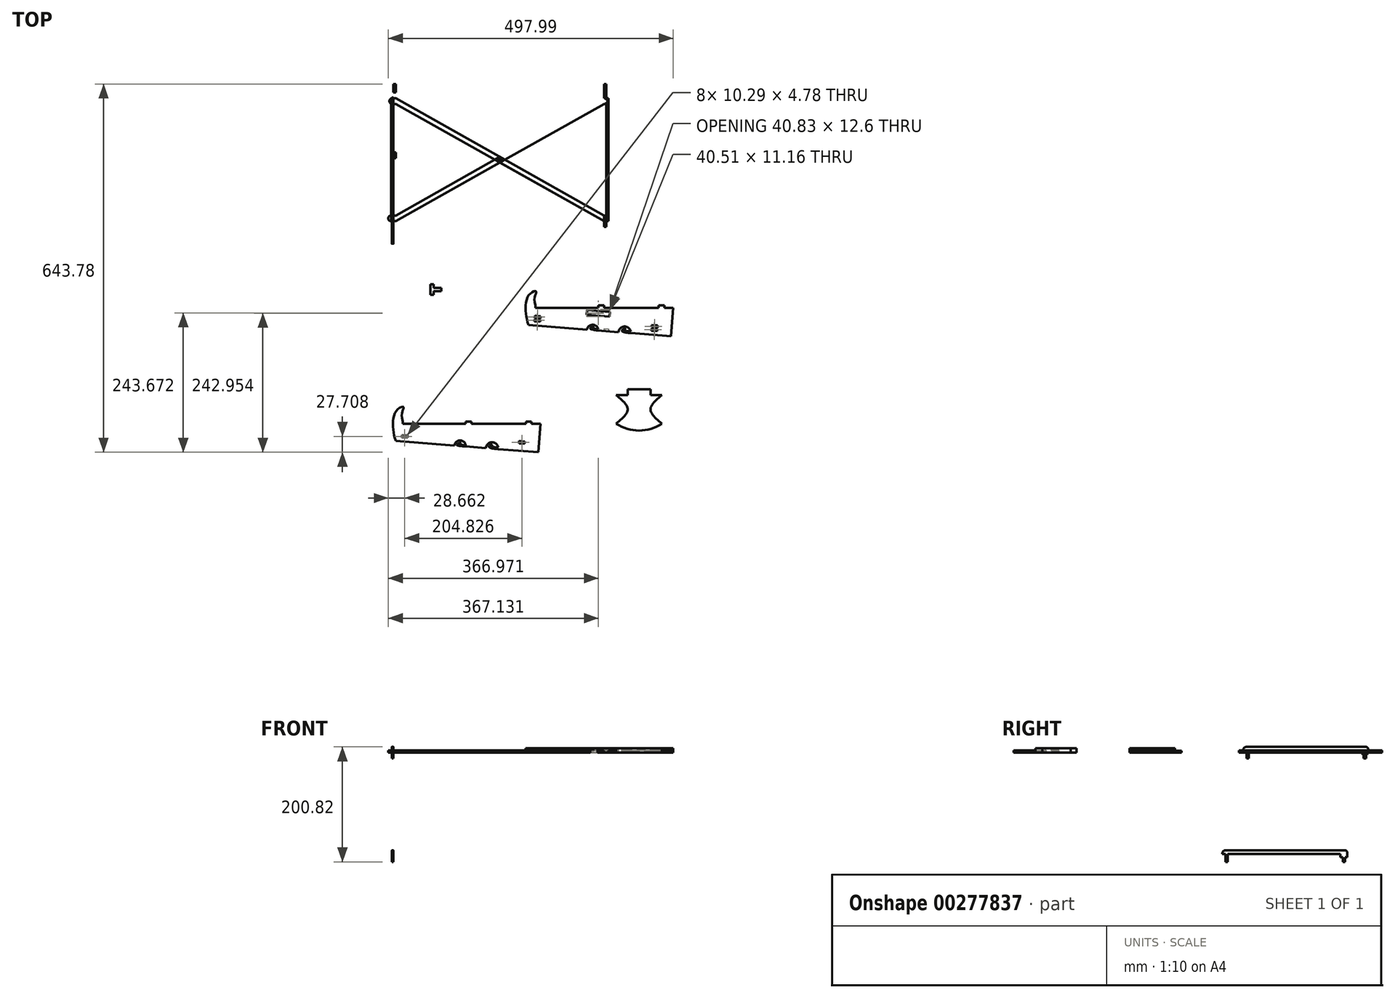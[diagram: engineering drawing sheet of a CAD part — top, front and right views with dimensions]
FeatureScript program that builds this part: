
annotation { "Feature Type Name" : "Feature", "Feature Type Description" : "" }
export const myFeature = defineFeature(function(context is Context, id is Id, definition is map)
    precondition{}
    {
        {
            var Q0;
            Q0=qCreatedBy(makeId("Top.planeOp"),FACE);
            var sketch = newSketch(context, id + "F0", { "sketchPlane" : qUnion([Q0])});
            skLineSegment(sketch, "E0.bottom", {"start": v(190, 125) * mm, "end": v(-190, 125) * mm});
            skLineSegment(sketch, "E0.top", {"start": v(190, -125) * mm, "end": v(-190, -125) * mm});
            skLineSegment(sketch, "E0.left", {"start": v(190, 125) * mm, "end": v(190, -125) * mm});
            skLineSegment(sketch, "E0.right", {"start": v(-190, 125) * mm, "end": v(-190, -125) * mm});
            skPoint(sketch, "E0.middle", {"position": v(0, 0) * mm});
            skLineSegment(sketch, "E1.right", {"start": v(-190, 125) * mm, "end": v(-190, -108) * mm});
            skLineSegment(sketch, "E2.bottom", {"start": v(-190, -125) * mm, "end": v(-186, -125) * mm});
            skLineSegment(sketch, "E2.top", {"start": v(-190, 125) * mm, "end": v(-186, 125) * mm});
            skLineSegment(sketch, "E2.left", {"start": v(-190, -125) * mm, "end": v(-190, -112) * mm});
            skLineSegment(sketch, "E2.right", {"start": v(-186, -125) * mm, "end": v(-186, -115) * mm});
            skLineSegment(sketch, "E3.bottom", {"start": v(190, -125) * mm, "end": v(186, -125) * mm});
            skLineSegment(sketch, "E3.top", {"start": v(190, 125) * mm, "end": v(186, 125) * mm});
            skLineSegment(sketch, "E3.left", {"start": v(190, -125) * mm, "end": v(190, 125) * mm});
            skLineSegment(sketch, "E3.right", {"start": v(186, -125) * mm, "end": v(186, 125) * mm});
            skLineSegment(sketch, "E4", {"start": v(49.8, -296.15) * mm, "end": v(152.32, -304.35) * mm});
            skLineSegment(sketch, "E5", {"start": v(299, -316.08) * mm, "end": v(303, -266.24) * mm});
            skLineSegment(sketch, "E6", {"start": v(303, -266.24) * mm, "end": v(287.2, -266.24) * mm});
            skLineSegment(sketch, "E7", {"start": v(52.2, -266.24) * mm, "end": v(49.8, -296.15) * mm, "construction": true});
            skLineSegment(sketch, "E8", {"start": v(0, 0) * mm, "end": v(0, 125) * mm, "construction": true});
            skLineSegment(sketch, "E9", {"start": v(0, 0) * mm, "end": v(0, -125) * mm, "construction": true});
            skLineSegment(sketch, "E10.bottom", {"start": v(-186, 125) * mm, "end": v(-182, 125) * mm});
            skLineSegment(sketch, "E10.top", {"start": v(-186, -125) * mm, "end": v(-182, -125) * mm});
            skLineSegment(sketch, "E10.left", {"start": v(-186, 125) * mm, "end": v(-186, 100) * mm});
            skLineSegment(sketch, "E10.right", {"start": v(-182, 125) * mm, "end": v(-182, 100) * mm});
            skLineSegment(sketch, "E11.MirrorCS", {"start": v(182, 125) * mm, "end": v(182, -125) * mm});
            skLineSegment(sketch, "E12", {"start": v(-186, -115) * mm, "end": v(-182, -115) * mm});
            skLineSegment(sketch, "E13", {"start": v(-186, 0) * mm, "end": v(186, 0) * mm, "construction": true});
            skLineSegment(sketch, "E14", {"start": v(-183.8, 0) * mm, "end": v(-183.8, 5) * mm, "construction": true});
            skLineSegment(sketch, "E15", {"start": v(-186, 5) * mm, "end": v(-182, 5) * mm});
            skLineSegment(sketch, "E16.MirrorCS", {"start": v(-186, -5) * mm, "end": v(-182, -5) * mm});
            skLineSegment(sketch, "E17", {"start": v(-186, 110) * mm, "end": v(-182, 110) * mm});
            skLineSegment(sketch, "E18", {"start": v(-186, 100) * mm, "end": v(-182, 100) * mm});
            skLineSegment(sketch, "E19", {"start": v(52.2, -266.24) * mm, "end": v(52.2, -242.24) * mm, "construction": true});
            skLineSegment(sketch, "E20", {"start": v(52.2, -242.24) * mm, "end": v(62.16, -243.04) * mm, "construction": true});
            skLineSegment(sketch, "E21", {"start": v(62.16, -243.04) * mm, "end": v(62.16, -266.24) * mm, "construction": true});
            skLineSegment(sketch, "E22.bottom", {"start": v(62.16, -266.24) * mm, "end": v(172.2, -266.24) * mm, "construction": true});
            skLineSegment(sketch, "E22.top", {"start": v(52.2, -262.24) * mm, "end": v(303, -262.24) * mm, "construction": true});
            skLineSegment(sketch, "E22.left", {"start": v(52.2, -266.24) * mm, "end": v(52.2, -262.24) * mm, "construction": true});
            skLineSegment(sketch, "E22.right", {"start": v(303, -266.24) * mm, "end": v(303, -262.24) * mm, "construction": true});
            skFitSpline(sketch, "E23", {"points": [v(49.8, -296.15) * mm, v(44.72, -265.8) * mm, v(52.2, -242.24) * mm, v(62.86, -237.24) * mm, v(62.38, -242.24) * mm, v(62.16, -262.24) * mm], "startDerivative": vector(-32.9, 108.57) * mm, "endDerivative": vector(52.9, -154.73) * mm});
            skLineSegment(sketch, "E24", {"start": v(62.16, -262.24) * mm, "end": v(62.16, -266.24) * mm});
            skLineSegment(sketch, "E25", {"start": v(302.2, -266.24) * mm, "end": v(302.2, -262.24) * mm, "construction": true});
            skLineSegment(sketch, "E26", {"start": v(287.2, -266.24) * mm, "end": v(287.2, -262.24) * mm});
            skLineSegment(sketch, "E27", {"start": v(287.2, -262.24) * mm, "end": v(277.2, -262.24) * mm});
            skLineSegment(sketch, "E28", {"start": v(277.2, -262.24) * mm, "end": v(277.2, -266.24) * mm});
            skLineSegment(sketch, "E29", {"start": v(182.2, -266.24) * mm, "end": v(182.2, -262.24) * mm});
            skLineSegment(sketch, "E30", {"start": v(172.2, -266.24) * mm, "end": v(172.2, -262.24) * mm});
            skLineSegment(sketch, "E31", {"start": v(172.2, -262.24) * mm, "end": v(182.2, -262.24) * mm});
            skLineSegment(sketch, "E32", {"start": v(-182, -105) * mm, "end": v(-186, -105) * mm});
            skLineSegment(sketch, "E33", {"start": v(-186, 90) * mm, "end": v(-182, 90) * mm});
            skLineSegment(sketch, "E34.MirrorCS", {"start": v(186, 125) * mm, "end": v(182, 125) * mm});
            skLineSegment(sketch, "E35.MirrorCS", {"start": v(186, -125) * mm, "end": v(182, -125) * mm});
            skLineSegment(sketch, "E36.MirrorCS", {"start": v(-190, -125) * mm, "end": v(190, -125) * mm});
            skLineSegment(sketch, "E37.MirrorCS", {"start": v(186, 110) * mm, "end": v(182, 110) * mm});
            skLineSegment(sketch, "E38.MirrorCS", {"start": v(183.8, 0) * mm, "end": v(183.8, 5) * mm, "construction": true});
            skLineSegment(sketch, "E39.MirrorCS", {"start": v(186, 100) * mm, "end": v(182, 100) * mm});
            skLineSegment(sketch, "E40.MirrorCS", {"start": v(182, -105) * mm, "end": v(186, -105) * mm});
            skLineSegment(sketch, "E41.MirrorCS", {"start": v(186, -5) * mm, "end": v(182, -5) * mm});
            skLineSegment(sketch, "E42.MirrorCS", {"start": v(186, 90) * mm, "end": v(182, 90) * mm});
            skLineSegment(sketch, "E43.MirrorCS", {"start": v(186, 5) * mm, "end": v(182, 5) * mm});
            skLineSegment(sketch, "E44.MirrorCS", {"start": v(186, -115) * mm, "end": v(182, -115) * mm});
            skLineSegment(sketch, "E45", {"start": v(-182, -115) * mm, "end": v(182, 90) * mm});
            skLineSegment(sketch, "E46", {"start": v(-182, -105) * mm, "end": v(182, 100) * mm});
            skLineSegment(sketch, "E47", {"start": v(-182, 90) * mm, "end": v(182, -115) * mm});
            skLineSegment(sketch, "E48", {"start": v(182, -105) * mm, "end": v(-182, 100) * mm});
            skLineSegment(sketch, "E49.trimOffspring", {"start": v(-186, -115) * mm, "end": v(-186, -125) * mm});
            skLineSegment(sketch, "E50.trimOffspring", {"start": v(-186, -105) * mm, "end": v(-186, 90) * mm});
            skLineSegment(sketch, "E51", {"start": v(-186, -105) * mm, "end": v(-190, -105) * mm});
            skLineSegment(sketch, "E52", {"start": v(-186, -115) * mm, "end": v(-190, -115) * mm});
            skArc(sketch, "E53", {"start": v(-190, -105) * mm, "mid": v(-195, -110) * mm, "end": v(-190, -115) * mm});
            skArc(sketch, "E54", {"start": v(-190, 99.76) * mm, "mid": v(-193.01, 94.84) * mm, "end": v(-190, 89.93) * mm});
            skLineSegment(sketch, "E55.trimOffspring", {"start": v(-186, 100) * mm, "end": v(-186, 125) * mm});
            skLineSegment(sketch, "E56.trimOffspring", {"start": v(-186, 90) * mm, "end": v(-186, -105) * mm});
            skLineSegment(sketch, "E57.trimOffspring", {"start": v(-182, 90) * mm, "end": v(-182, -125) * mm});
            skLineSegment(sketch, "E58.MirrorCS", {"start": v(186, -125) * mm, "end": v(186, -115) * mm});
            skLineSegment(sketch, "E59.MirrorCS", {"start": v(186, -115) * mm, "end": v(186, -125) * mm});
            skLineSegment(sketch, "E60.MirrorCS", {"start": v(186, -115) * mm, "end": v(190, -115) * mm});
            skLineSegment(sketch, "E61.MirrorCS", {"start": v(186, -105) * mm, "end": v(190, -105) * mm});
            skArc(sketch, "E62.MirrorCS", {"start": v(190, -105) * mm, "mid": v(195, -110) * mm, "end": v(190, -115) * mm});
            skLineSegment(sketch, "E63.MirrorCS", {"start": v(186, 100) * mm, "end": v(186, 125) * mm});
            skLineSegment(sketch, "E64.MirrorCS", {"start": v(182, 125) * mm, "end": v(182, 100) * mm});
            skLineSegment(sketch, "E65.MirrorCS", {"start": v(186, 125) * mm, "end": v(186, 100) * mm});
            skArc(sketch, "E66.MirrorCS", {"start": v(190, 99.76) * mm, "mid": v(193.01, 94.84) * mm, "end": v(190, 89.93) * mm});
            skLineSegment(sketch, "E67.MirrorCS", {"start": v(186, 90) * mm, "end": v(186, -105) * mm});
            skLineSegment(sketch, "E68.MirrorCS", {"start": v(186, -105) * mm, "end": v(186, 90) * mm});
            skLineSegment(sketch, "E69.MirrorCS", {"start": v(182, 90) * mm, "end": v(182, -125) * mm});
            skLineSegment(sketch, "E70", {"start": v(186, 100) * mm, "end": v(190, 99.76) * mm});
            skLineSegment(sketch, "E71", {"start": v(186, 90) * mm, "end": v(190, 89.93) * mm});
            skLineSegment(sketch, "E72", {"start": v(-186, 90) * mm, "end": v(-190, 89.93) * mm});
            skLineSegment(sketch, "E73", {"start": v(-186, 100) * mm, "end": v(-190, 99.76) * mm});
            skLineSegment(sketch, "E74.trimOffspring", {"start": v(182.2, -266.24) * mm, "end": v(277.2, -266.24) * mm, "construction": true});
            skLineSegment(sketch, "E75.trimOffspring", {"start": v(172.2, -266.24) * mm, "end": v(62.16, -266.24) * mm});
            skLineSegment(sketch, "E76.trimOffspring", {"start": v(287.2, -266.24) * mm, "end": v(303, -266.24) * mm, "construction": true});
            skLineSegment(sketch, "E77.trimOffspring", {"start": v(277.2, -266.24) * mm, "end": v(182.2, -266.24) * mm});
            skLineSegment(sketch, "E78", {"start": v(50.88, -283.2) * mm, "end": v(70.77, -284.78) * mm, "construction": true});
            skLineSegment(sketch, "E79", {"start": v(51.2, -279.2) * mm, "end": v(61.13, -280) * mm, "construction": true});
            skLineSegment(sketch, "E80", {"start": v(275.12, -301.13) * mm, "end": v(275.44, -297.14) * mm});
            skLineSegment(sketch, "E81", {"start": v(275.44, -297.14) * mm, "end": v(265.47, -296.35) * mm});
            skLineSegment(sketch, "E82", {"start": v(265.47, -296.35) * mm, "end": v(265.15, -300.33) * mm});
            skLineSegment(sketch, "E83", {"start": v(265.15, -300.33) * mm, "end": v(275.12, -301.13) * mm});
            skLineSegment(sketch, "E84", {"start": v(60.8, -283.99) * mm, "end": v(61.13, -280) * mm});
            skLineSegment(sketch, "E85", {"start": v(71.1, -280.8) * mm, "end": v(70.77, -284.78) * mm});
            skLineSegment(sketch, "E86", {"start": v(61.13, -280) * mm, "end": v(71.1, -280.8) * mm});
            skLineSegment(sketch, "E87", {"start": v(70.77, -284.78) * mm, "end": v(60.8, -283.99) * mm});
            skLineSegment(sketch, "E88", {"start": v(265.47, -296.35) * mm, "end": v(264.12, -313.3) * mm, "construction": true});
            skLineSegment(sketch, "E89", {"start": v(275.44, -297.14) * mm, "end": v(274.09, -314.1) * mm, "construction": true});
            skLineSegment(sketch, "E90", {"start": v(264.68, -306.32) * mm, "end": v(274.64, -307.11) * mm});
            skLineSegment(sketch, "E91", {"start": v(265, -302.33) * mm, "end": v(274.96, -303.13) * mm});
            skLineSegment(sketch, "E92", {"start": v(265, -302.33) * mm, "end": v(264.68, -306.32) * mm});
            skLineSegment(sketch, "E93", {"start": v(274.96, -303.13) * mm, "end": v(274.64, -307.11) * mm});
            skLineSegment(sketch, "E94", {"start": v(61.13, -280) * mm, "end": v(59.77, -296.95) * mm, "construction": true});
            skLineSegment(sketch, "E95", {"start": v(60.65, -285.98) * mm, "end": v(70.62, -286.78) * mm});
            skLineSegment(sketch, "E96", {"start": v(60.33, -289.97) * mm, "end": v(70.3, -290.77) * mm});
            skLineSegment(sketch, "E97", {"start": v(70.3, -290.77) * mm, "end": v(70.62, -286.78) * mm});
            skLineSegment(sketch, "E98", {"start": v(60.65, -285.98) * mm, "end": v(60.33, -289.97) * mm});
            skLineSegment(sketch, "E99", {"start": v(-182, -498.85) * mm, "end": v(-79.55, -507.04) * mm});
            skLineSegment(sketch, "E100", {"start": v(67.2, -518.78) * mm, "end": v(71.18, -468.94) * mm});
            skLineSegment(sketch, "E101", {"start": v(71.18, -468.94) * mm, "end": v(55.38, -468.94) * mm});
            skLineSegment(sketch, "E102", {"start": v(-179.62, -468.94) * mm, "end": v(-182, -498.85) * mm, "construction": true});
            skLineSegment(sketch, "E103", {"start": v(-179.62, -468.94) * mm, "end": v(-179.62, -444.94) * mm, "construction": true});
            skLineSegment(sketch, "E104", {"start": v(-179.62, -444.94) * mm, "end": v(-169.65, -445.74) * mm, "construction": true});
            skLineSegment(sketch, "E105", {"start": v(-169.65, -445.74) * mm, "end": v(-169.65, -468.94) * mm, "construction": true});
            skLineSegment(sketch, "E106.bottom", {"start": v(-169.65, -468.94) * mm, "end": v(-59.62, -468.94) * mm, "construction": true});
            skLineSegment(sketch, "E106.top", {"start": v(-179.62, -464.94) * mm, "end": v(71.18, -464.94) * mm, "construction": true});
            skLineSegment(sketch, "E106.left", {"start": v(-179.62, -468.94) * mm, "end": v(-179.62, -464.94) * mm, "construction": true});
            skLineSegment(sketch, "E106.right", {"start": v(71.18, -468.94) * mm, "end": v(71.18, -464.94) * mm, "construction": true});
            skFitSpline(sketch, "E107", {"points": [v(-182, -498.85) * mm, v(-187.09, -467.99) * mm, v(-179.62, -444.94) * mm, v(-168.95, -439.42) * mm, v(-169.43, -444.94) * mm, v(-169.65, -464.94) * mm], "startDerivative": vector(-32.9, 108.57) * mm, "endDerivative": vector(52.9, -154.73) * mm});
            skLineSegment(sketch, "E108", {"start": v(-169.65, -464.94) * mm, "end": v(-169.65, -468.94) * mm});
            skLineSegment(sketch, "E109", {"start": v(70.38, -468.94) * mm, "end": v(70.38, -464.94) * mm, "construction": true});
            skLineSegment(sketch, "E110", {"start": v(55.38, -468.94) * mm, "end": v(55.38, -464.94) * mm});
            skLineSegment(sketch, "E111", {"start": v(55.38, -464.94) * mm, "end": v(45.38, -464.94) * mm});
            skLineSegment(sketch, "E112", {"start": v(45.38, -464.94) * mm, "end": v(45.38, -468.94) * mm});
            skLineSegment(sketch, "E113", {"start": v(-49.62, -468.94) * mm, "end": v(-49.62, -464.94) * mm});
            skLineSegment(sketch, "E114", {"start": v(-59.62, -468.94) * mm, "end": v(-59.62, -464.94) * mm});
            skLineSegment(sketch, "E115", {"start": v(-59.62, -464.94) * mm, "end": v(-49.62, -464.94) * mm});
            skLineSegment(sketch, "E116.trimOffspring", {"start": v(-49.62, -468.94) * mm, "end": v(45.38, -468.94) * mm, "construction": true});
            skLineSegment(sketch, "E117.trimOffspring", {"start": v(-59.62, -468.94) * mm, "end": v(-169.65, -468.94) * mm});
            skLineSegment(sketch, "E118.trimOffspring", {"start": v(55.38, -468.94) * mm, "end": v(71.18, -468.94) * mm, "construction": true});
            skLineSegment(sketch, "E119.trimOffspring", {"start": v(45.38, -468.94) * mm, "end": v(-49.62, -468.94) * mm});
            skLineSegment(sketch, "E120", {"start": v(-180.97, -485.89) * mm, "end": v(68.23, -505.82) * mm, "construction": true});
            skLineSegment(sketch, "E121", {"start": v(-180.65, -481.9) * mm, "end": v(68.55, -501.84) * mm, "construction": true});
            skLineSegment(sketch, "E122", {"start": v(43.31, -503.83) * mm, "end": v(43.63, -499.84) * mm});
            skLineSegment(sketch, "E123", {"start": v(43.63, -499.84) * mm, "end": v(33.66, -499.05) * mm});
            skLineSegment(sketch, "E124", {"start": v(33.66, -499.05) * mm, "end": v(33.34, -503.03) * mm});
            skLineSegment(sketch, "E125", {"start": v(33.34, -503.03) * mm, "end": v(43.31, -503.83) * mm});
            skLineSegment(sketch, "E126", {"start": v(-171, -486.69) * mm, "end": v(-170.68, -482.7) * mm});
            skLineSegment(sketch, "E127", {"start": v(-160.72, -483.5) * mm, "end": v(-161.03, -487.48) * mm});
            skLineSegment(sketch, "E128", {"start": v(-170.68, -482.7) * mm, "end": v(-160.72, -483.5) * mm});
            skLineSegment(sketch, "E129", {"start": v(-161.03, -487.48) * mm, "end": v(-171, -486.69) * mm});
            skLineSegment(sketch, "E130", {"start": v(33.66, -499.05) * mm, "end": v(32.3, -516) * mm, "construction": true});
            skLineSegment(sketch, "E131", {"start": v(43.63, -499.84) * mm, "end": v(42.28, -516.79) * mm, "construction": true});
            skLineSegment(sketch, "E132", {"start": v(32.87, -509.01) * mm, "end": v(42.83, -509.81) * mm});
            skLineSegment(sketch, "E133", {"start": v(33.19, -505.03) * mm, "end": v(43.15, -505.82) * mm});
            skLineSegment(sketch, "E134", {"start": v(33.19, -505.03) * mm, "end": v(32.87, -509.01) * mm});
            skLineSegment(sketch, "E135", {"start": v(43.15, -505.82) * mm, "end": v(42.83, -509.81) * mm});
            skLineSegment(sketch, "E136", {"start": v(-170.68, -482.7) * mm, "end": v(-172.04, -499.64) * mm, "construction": true});
            skLineSegment(sketch, "E137", {"start": v(-171.16, -488.68) * mm, "end": v(-161.2, -489.48) * mm});
            skLineSegment(sketch, "E138", {"start": v(-171.48, -492.67) * mm, "end": v(-161.51, -493.46) * mm});
            skLineSegment(sketch, "E139", {"start": v(-161.51, -493.46) * mm, "end": v(-161.2, -489.48) * mm});
            skLineSegment(sketch, "E140", {"start": v(-171.16, -488.68) * mm, "end": v(-171.48, -492.67) * mm});
            skLineSegment(sketch, "E141.MirrorCS", {"start": v(-190, -125) * mm, "end": v(-190, 125) * mm});
            skLineSegment(sketch, "E142.trimOffspring", {"start": v(-190, -108) * mm, "end": v(-190, 125) * mm});
            skLineSegment(sketch, "E143.trimOffspring", {"start": v(-190, -110) * mm, "end": v(-190, -125) * mm});
            skLineSegment(sketch, "E144.bottom", {"start": v(-189, 96.84) * mm, "end": v(-186, 96.84) * mm, "construction": true});
            skLineSegment(sketch, "E144.top", {"start": v(-189, 92.84) * mm, "end": v(-186, 92.84) * mm, "construction": true});
            skLineSegment(sketch, "E144.left", {"start": v(-189, 96.84) * mm, "end": v(-189, 92.84) * mm, "construction": true});
            skLineSegment(sketch, "E144.right", {"start": v(-186, 96.84) * mm, "end": v(-186, 92.84) * mm, "construction": true});
            skLineSegment(sketch, "E145.MirrorCS", {"start": v(189, 92.84) * mm, "end": v(186, 92.84) * mm});
            skLineSegment(sketch, "E146.MirrorCS", {"start": v(189, 96.84) * mm, "end": v(186, 96.84) * mm});
            skLineSegment(sketch, "E147.MirrorCS", {"start": v(189, 96.84) * mm, "end": v(189, 92.84) * mm});
            skLineSegment(sketch, "E148.MirrorCS", {"start": v(186, 96.84) * mm, "end": v(186, 92.84) * mm});
            skLineSegment(sketch, "E149.bottom", {"start": v(-186.1, -112) * mm, "end": v(-189.1, -112) * mm});
            skLineSegment(sketch, "E149.top", {"start": v(-186.1, -108) * mm, "end": v(-189.1, -108) * mm});
            skLineSegment(sketch, "E149.left", {"start": v(-186.1, -112) * mm, "end": v(-186.1, -108) * mm});
            skLineSegment(sketch, "E149.right", {"start": v(-189.1, -112) * mm, "end": v(-189.1, -108) * mm});
            skLineSegment(sketch, "E150", {"start": v(-186, -105) * mm, "end": v(-186, -115) * mm, "construction": true});
            skLineSegment(sketch, "E151.MirrorCS", {"start": v(190, -108) * mm, "end": v(190, 125) * mm});
            skLineSegment(sketch, "E152.MirrorCS", {"start": v(190, -110) * mm, "end": v(190, -125) * mm});
            skLineSegment(sketch, "E153.MirrorCS", {"start": v(186, -105) * mm, "end": v(186, -115) * mm, "construction": true});
            skLineSegment(sketch, "E154.MirrorCS", {"start": v(190, 125) * mm, "end": v(190, -108) * mm});
            skLineSegment(sketch, "E155.MirrorCS", {"start": v(186.1, -112) * mm, "end": v(189.1, -112) * mm});
            skLineSegment(sketch, "E156.MirrorCS", {"start": v(190, -125) * mm, "end": v(190, -112) * mm});
            skLineSegment(sketch, "E157.MirrorCS", {"start": v(186.1, -112) * mm, "end": v(186.1, -108) * mm});
            skLineSegment(sketch, "E158.MirrorCS", {"start": v(189.1, -112) * mm, "end": v(189.1, -108) * mm});
            skLineSegment(sketch, "E159.MirrorCS", {"start": v(186.1, -108) * mm, "end": v(189.1, -108) * mm});
            skLineSegment(sketch, "E160", {"start": v(-186, 90) * mm, "end": v(-186, 100) * mm, "construction": true});
            skLineSegment(sketch, "E161.bottom", {"start": v(-189, 96.84) * mm, "end": v(-186, 96.84) * mm});
            skLineSegment(sketch, "E161.top", {"start": v(-189, 92.84) * mm, "end": v(-186, 92.84) * mm});
            skLineSegment(sketch, "E161.left", {"start": v(-189, 96.84) * mm, "end": v(-189, 92.84) * mm});
            skLineSegment(sketch, "E161.right", {"start": v(-186, 96.84) * mm, "end": v(-186, 92.84) * mm});
            skLineSegment(sketch, "E162", {"start": v(8.88, -7.5) * mm, "end": v(-8.88, -7.5) * mm, "construction": true});
            skLineSegment(sketch, "E163.bottom", {"start": v(3, -9) * mm, "end": v(-3, -9) * mm});
            skLineSegment(sketch, "E163.top", {"start": v(3, -6) * mm, "end": v(-3, -6) * mm});
            skLineSegment(sketch, "E163.left", {"start": v(3, -9) * mm, "end": v(3, -6) * mm});
            skLineSegment(sketch, "E163.right", {"start": v(-3, -9) * mm, "end": v(-3, -6) * mm});
            skPoint(sketch, "E163.middle", {"position": v(0, -7.5) * mm});
            skLineSegment(sketch, "E164.bottom", {"start": v(-115.58, -237.46) * mm, "end": v(-102.58, -237.46) * mm});
            skLineSegment(sketch, "E164.top", {"start": v(-115.58, -231.46) * mm, "end": v(-102.58, -231.46) * mm});
            skLineSegment(sketch, "E164.left", {"start": v(-121.58, -237.46) * mm, "end": v(-121.58, -231.46) * mm});
            skLineSegment(sketch, "E164.right", {"start": v(-102.58, -237.46) * mm, "end": v(-102.58, -231.46) * mm});
            skPoint(sketch, "E164.middle", {"position": v(-112.08, -234.46) * mm});
            skLineSegment(sketch, "E165.top", {"start": v(-121.58, -243.46) * mm, "end": v(-115.58, -243.46) * mm});
            skLineSegment(sketch, "E165.left", {"start": v(-121.58, -231.46) * mm, "end": v(-121.58, -243.46) * mm});
            skLineSegment(sketch, "E165.right", {"start": v(-115.58, -237.46) * mm, "end": v(-115.58, -243.46) * mm});
            skLineSegment(sketch, "E166", {"start": v(-105.58, -231.46) * mm, "end": v(-105.58, -237.46) * mm, "construction": true});
            skLineSegment(sketch, "E167", {"start": v(-121.58, -231.46) * mm, "end": v(-121.58, -225.46) * mm});
            skLineSegment(sketch, "E168", {"start": v(-121.58, -225.46) * mm, "end": v(-115.58, -225.46) * mm});
            skLineSegment(sketch, "E169", {"start": v(-115.58, -225.46) * mm, "end": v(-115.58, -231.46) * mm});
            skLineSegment(sketch, "E170", {"start": v(191.59, -281.4) * mm, "end": v(151.72, -278.22) * mm});
            skLineSegment(sketch, "E171", {"start": v(151.72, -278.22) * mm, "end": v(152.35, -270.24) * mm});
            skLineSegment(sketch, "E172", {"start": v(152.35, -270.24) * mm, "end": v(192.23, -273.43) * mm});
            skLineSegment(sketch, "E173", {"start": v(192.23, -273.43) * mm, "end": v(191.59, -281.4) * mm});
            skLineSegment(sketch, "E174.trimOffspring", {"start": v(237.81, -294.13) * mm, "end": v(300.4, -299.14) * mm, "construction": true});
            skLineSegment(sketch, "E175", {"start": v(181.86, -302.7) * mm, "end": v(189.85, -303.34) * mm});
            skLineSegment(sketch, "E176", {"start": v(181.54, -306.69) * mm, "end": v(197.49, -307.96) * mm});
            skLineSegment(sketch, "E177", {"start": v(181.86, -302.7) * mm, "end": v(181.54, -306.69) * mm});
            skLineSegment(sketch, "E178.bottom", {"start": v(223.2, -408.84) * mm, "end": v(263.2, -408.84) * mm});
            skLineSegment(sketch, "E178.left", {"start": v(223.2, -408.84) * mm, "end": v(223.2, -418.84) * mm});
            skLineSegment(sketch, "E178.right", {"start": v(263.2, -408.84) * mm, "end": v(263.2, -418.84) * mm});
            skLineSegment(sketch, "E179", {"start": v(263.2, -418.84) * mm, "end": v(283.2, -418.84) * mm});
            skLineSegment(sketch, "E180", {"start": v(223.2, -418.84) * mm, "end": v(203.2, -418.84) * mm});
            skFitSpline(sketch, "E181", {"points": [v(203.2, -418.84) * mm, v(223.2, -443.84) * mm, v(203.2, -468.84) * mm], "startDerivative": vector(60, -50) * mm, "endDerivative": vector(-60, -50) * mm});
            skLineSegment(sketch, "E182", {"start": v(243.2, -408.84) * mm, "end": v(243.2, -468.84) * mm, "construction": true});
            skFitSpline(sketch, "E183.MirrorCS", {"points": [v(283.2, -418.84) * mm, v(263.2, -443.84) * mm, v(283.2, -468.84) * mm], "startDerivative": vector(-60, -50) * mm, "endDerivative": vector(60, -50) * mm});
            skArc(sketch, "E184", {"start": v(203.2, -468.84) * mm, "mid": v(243.2, -480.84) * mm, "end": v(283.2, -468.84) * mm});
            skLineSegment(sketch, "E185", {"start": v(186.56, -268.97) * mm, "end": v(184.57, -268.8) * mm});
            skLineSegment(sketch, "E186", {"start": v(192.23, -273.43) * mm, "end": v(192.55, -269.45) * mm});
            skLineSegment(sketch, "E187", {"start": v(192.55, -269.45) * mm, "end": v(186.56, -268.97) * mm});
            skLineSegment(sketch, "E188", {"start": v(184.57, -268.8) * mm, "end": v(184.25, -272.8) * mm});
            skLineSegment(sketch, "E189", {"start": v(172.2, -266.24) * mm, "end": v(172.2, -279.86) * mm, "construction": true});
            skArc(sketch, "E190", {"start": v(171.92, -303.6) * mm, "mid": v(161.81, -295.95) * mm, "end": v(152.32, -304.35) * mm});
            skLineSegment(sketch, "E191", {"start": v(-59.62, -468.94) * mm, "end": v(-59.62, -507.28) * mm, "construction": true});
            skArc(sketch, "E192", {"start": v(-2.9, -510.02) * mm, "mid": v(-14.37, -501.34) * mm, "end": v(-24.62, -511.44) * mm});
            skLineSegment(sketch, "E193.trimOffspring", {"start": v(-59.62, -508.64) * mm, "end": v(-24.62, -511.44) * mm});
            skLineSegment(sketch, "E194.trimOffspring", {"start": v(-2.69, -513.2) * mm, "end": v(67.2, -518.78) * mm});
            skFitSpline(sketch, "E195", {"points": [v(-2.69, -513.2) * mm, v(-15.78, -511.43) * mm, v(-19.23, -509.19) * mm, v(-17.76, -506.59) * mm, v(-13.38, -506.25) * mm, v(-14.8, -508.21) * mm, v(-2.69, -511.44) * mm], "startDerivative": vector(-44.09, 4) * mm, "endDerivative": vector(41.48, -21.36) * mm});
            skFitSpline(sketch, "E196", {"points": [v(-59.62, -508.64) * mm, v(-75.41, -506.11) * mm, v(-74.67, -504.74) * mm, v(-71.74, -503.03) * mm, v(-68.32, -502.54) * mm, v(-68.95, -504.77) * mm, v(-59.72, -506.6) * mm], "startDerivative": vector(-44.09, 4) * mm, "endDerivative": vector(48.5, -6.14) * mm});
            skArc(sketch, "E197.trimOffspring", {"start": v(-59.72, -506.6) * mm, "mid": v(-69.83, -498.12) * mm, "end": v(-79.55, -507.04) * mm});
            skFitSpline(sketch, "E198", {"points": [v(172.13, -305.97) * mm, v(161.88, -304.33) * mm, v(157.84, -302.36) * mm, v(159.8, -299.35) * mm, v(163.27, -298.58) * mm, v(162.56, -301.53) * mm, v(172.2, -303.64) * mm], "startDerivative": vector(-44.09, 4) * mm, "endDerivative": vector(48.5, -6.14) * mm});
            skLineSegment(sketch, "E199.trimOffspring", {"start": v(170.42, -305.8) * mm, "end": v(207.13, -308.73) * mm});
            skArc(sketch, "E200", {"start": v(228.8, -307.7) * mm, "mid": v(217.53, -299.03) * mm, "end": v(207.13, -308.73) * mm});
            skFitSpline(sketch, "E201", {"points": [v(229.05, -310.49) * mm, v(216.5, -308.58) * mm, v(212.99, -306.61) * mm, v(215.8, -303.95) * mm, v(219.36, -302.92) * mm, v(218.14, -305.54) * mm, v(229.73, -307.84) * mm], "startDerivative": vector(-44.09, 4) * mm, "endDerivative": vector(48.04, -9.09) * mm});
            skLineSegment(sketch, "E202.trimOffspring", {"start": v(229.05, -310.49) * mm, "end": v(299, -316.08) * mm});
            skLineSegment(sketch, "E203", {"start": v(-8.02, -510.02) * mm, "end": v(-2.9, -510.02) * mm});
            skLineSegment(sketch, "E204", {"start": v(-170.68, -482.7) * mm, "end": v(-169.97, -473.73) * mm, "construction": true});
            skLineSegment(sketch, "E205", {"start": v(-169.97, -473.73) * mm, "end": v(44.35, -490.87) * mm, "construction": true});
            skLineSegment(sketch, "E206", {"start": v(44.35, -490.87) * mm, "end": v(43.63, -499.84) * mm, "construction": true});
            skLineSegment(sketch, "E207", {"start": v(-169.97, -473.73) * mm, "end": v(-169.65, -468.94) * mm, "construction": true});
            skLineSegment(sketch, "E208.trimOffspring", {"start": v(189.83, -303.34) * mm, "end": v(189.52, -307.32) * mm});
            skLineSegment(sketch, "E209.trimOffspring", {"start": v(265.15, -300.33) * mm, "end": v(300.08, -303.13) * mm, "construction": true});
            skLineSegment(sketch, "E210.trimOffspring", {"start": v(172.2, -288.88) * mm, "end": v(197.94, -290.94) * mm, "construction": true});
            skLineSegment(sketch, "E211.trimOffspring", {"start": v(172.2, -288.88) * mm, "end": v(172.2, -305.94) * mm, "construction": true});
            skPoint(sketch, "E212.end.orphan", {"position": v(223.2, -468.84) * mm});
            skPoint(sketch, "E213.MirrorCS.end.orphan", {"position": v(263.2, -468.84) * mm});
            skLineSegment(sketch, "E214.trimOffspring", {"start": v(263.2, -418.84) * mm, "end": v(271.68, -418.84) * mm});
            skSolve(sketch);
        }
        {
            var Q0;
            {var subQ0=sQuery(id+"F0.wireOp",EDGE,"E42.MirrorCS");Q0=makeQuery(id+"F0.imprint","IMPRINT",FACE,{"disambiguationData":[TD([[makeQuery(id+"F0.imprint","IMPRINT",EDGE,{"derivedFrom":subQ0}),1.0]])]});}
            var Q1;
            {var subQ0=sQuery(id+"F0.wireOp",EDGE,"E47");var subQ1=sQuery(id+"F0.wireOp",EDGE,"E45");var subQ2=makeQuery(id+"F0.imprint","INTERSECT",VERTEX,{"derivedFrom":[subQ1,subQ0]});Q1=makeQuery(id+"F0.imprint","IMPRINT",FACE,{"disambiguationData":[TD([[makeQuery(id+"F0.imprint","IMPRINT",EDGE,{"disambiguationData":[TD([[subQ2,-1.0]])],"derivedFrom":subQ1}),-1.0]])]});}
            var Q2;
            {var subQ8=sQuery(id+"F0.wireOp",EDGE,"E0.bottom");Q2=makeQuery(id+"F0.imprint","IMPRINT",FACE,{"disambiguationData":[TD([[makeQuery(id+"F0.imprint","IMPRINT",EDGE,{"derivedFrom":subQ8}),1.0]])]});}
            var Q3;
            {var subQ14=sQuery(id+"F0.wireOp",EDGE,"E2.top");Q3=makeQuery(id+"F0.imprint","IMPRINT",FACE,{"disambiguationData":[TD([[makeQuery(id+"F0.imprint","IMPRINT",EDGE,{"derivedFrom":subQ14}),-1.0]])]});}
            var Q4;
            {var subQ0=sQuery(id+"F0.wireOp",EDGE,"E11.MirrorCS");Q4=makeQuery(id+"F0.imprint","IMPRINT",FACE,{"disambiguationData":[TD([[makeQuery(id+"F0.imprint","IMPRINT",EDGE,{"derivedFrom":subQ0}),-1.0]])]});}
            var Q5;
            {var subQ0=sQuery(id+"F0.wireOp",EDGE,"E40.MirrorCS");Q5=makeQuery(id+"F0.imprint","IMPRINT",FACE,{"disambiguationData":[TD([[makeQuery(id+"F0.imprint","IMPRINT",EDGE,{"derivedFrom":subQ0}),1.0]])]});}
            var Q6;
            {var subQ0=sQuery(id+"F0.wireOp",EDGE,"E15");Q6=makeQuery(id+"F0.imprint","IMPRINT",FACE,{"disambiguationData":[TD([[makeQuery(id+"F0.imprint","IMPRINT",EDGE,{"derivedFrom":subQ0}),1.0]])]});}
            var Q7;
            {var subQ0=sQuery(id+"F0.wireOp",EDGE,"E34.MirrorCS");Q7=makeQuery(id+"F0.imprint","IMPRINT",FACE,{"disambiguationData":[TD([[makeQuery(id+"F0.imprint","IMPRINT",EDGE,{"derivedFrom":subQ0}),1.0]])]});}
            var Q8;
            {var subQ0=sQuery(id+"F0.wireOp",EDGE,"E69.MirrorCS");var subQ3=makeQuery(id+"F0.imprint","INTERSECT",VERTEX,{"derivedFrom":[sQuery(id+"F0.wireOp",EDGE,"E43.MirrorCS"),subQ0]});Q8=makeQuery(id+"F0.imprint","IMPRINT",FACE,{"disambiguationData":[TD([[makeQuery(id+"F0.imprint","IMPRINT",EDGE,{"disambiguationData":[TD([[subQ3,-1.0]])],"derivedFrom":subQ0}),-1.0]])]});}
            var Q9;
            {var subQ0=sQuery(id+"F0.wireOp",EDGE,"E16.MirrorCS");Q9=makeQuery(id+"F0.imprint","IMPRINT",FACE,{"disambiguationData":[TD([[makeQuery(id+"F0.imprint","IMPRINT",EDGE,{"derivedFrom":subQ0}),-1.0]])]});}
            var Q10;
            {var subQ0=sQuery(id+"F0.wireOp",EDGE,"E10.bottom");Q10=makeQuery(id+"F0.imprint","IMPRINT",FACE,{"disambiguationData":[TD([[makeQuery(id+"F0.imprint","IMPRINT",EDGE,{"derivedFrom":subQ0}),-1.0]])]});}
            var Q11;
            {var subQ0=sQuery(id+"F0.wireOp",EDGE,"E57.trimOffspring");var subQ1=makeQuery(id+"F0.imprint","INTERSECT",VERTEX,{"derivedFrom":[sQuery(id+"F0.wireOp",EDGE,"E15"),subQ0]});Q11=makeQuery(id+"F0.imprint","IMPRINT",FACE,{"disambiguationData":[TD([[makeQuery(id+"F0.imprint","IMPRINT",EDGE,{"disambiguationData":[TD([[subQ1,-1.0]])],"derivedFrom":subQ0}),1.0]])]});}
            var Q12;
            {var subQ0=sQuery(id+"F0.wireOp",EDGE,"E57.trimOffspring");var subQ3=sQuery(id+"F0.wireOp",EDGE,"E36.MirrorCS");var subQ4=makeQuery(id+"F0.imprint","INTERSECT",VERTEX,{"derivedFrom":[subQ3,subQ0]});Q12=makeQuery(id+"F0.imprint","IMPRINT",FACE,{"disambiguationData":[TD([[makeQuery(id+"F0.imprint","IMPRINT",EDGE,{"disambiguationData":[TD([[subQ4,-1.0]])],"derivedFrom":subQ3}),1.0]])]});}
            var Q13;
            {var subQ1=sQuery(id+"F0.wireOp",EDGE,"E45");var subQ3=sQuery(id+"F0.wireOp",EDGE,"E47");var subQ4=makeQuery(id+"F0.imprint","INTERSECT",VERTEX,{"derivedFrom":[subQ1,subQ3]});Q13=makeQuery(id+"F0.imprint","IMPRINT",FACE,{"disambiguationData":[TD([[makeQuery(id+"F0.imprint","IMPRINT",EDGE,{"disambiguationData":[TD([[subQ4,1.0]])],"derivedFrom":subQ3}),-1.0]])]});}
            var Q14;
            {var subQ0=sQuery(id+"F0.wireOp",EDGE,"E47");var subQ1=sQuery(id+"F0.wireOp",EDGE,"E45");var subQ2=makeQuery(id+"F0.imprint","INTERSECT",VERTEX,{"derivedFrom":[subQ1,subQ0]});Q14=makeQuery(id+"F0.imprint","IMPRINT",FACE,{"disambiguationData":[TD([[makeQuery(id+"F0.imprint","IMPRINT",EDGE,{"disambiguationData":[TD([[subQ2,-1.0]])],"derivedFrom":subQ1}),1.0]])]});}
            var Q15;
            {var subQ1=sQuery(id+"F0.wireOp",EDGE,"E61.MirrorCS");Q15=makeQuery(id+"F0.imprint","IMPRINT",FACE,{"disambiguationData":[TD([[makeQuery(id+"F0.imprint","IMPRINT",EDGE,{"derivedFrom":subQ1}),1.0]])]});}
            var Q16;
            {var subQ1=sQuery(id+"F0.wireOp",EDGE,"E3.top");Q16=makeQuery(id+"F0.imprint","IMPRINT",FACE,{"disambiguationData":[TD([[makeQuery(id+"F0.imprint","IMPRINT",EDGE,{"derivedFrom":subQ1}),1.0]])]});}
            var Q17;
            {var subQ1=sQuery(id+"F0.wireOp",EDGE,"E12");Q17=makeQuery(id+"F0.imprint","IMPRINT",FACE,{"disambiguationData":[TD([[makeQuery(id+"F0.imprint","IMPRINT",EDGE,{"derivedFrom":subQ1}),1.0]])]});}
            var Q18;
            Q18=makeQuery(id+"F0.imprint","IMPRINT",FACE,{"disambiguationData":[TD([[makeQuery(id+"F0.imprint","IMPRINT",EDGE,{"derivedFrom":sQuery(id+"F0.wireOp",EDGE,"E11.MirrorCS")}),1.0]])]});
            var Q19;
            {var subQ4=sQuery(id+"F0.wireOp",EDGE,"E49.trimOffspring");Q19=makeQuery(id+"F0.imprint","IMPRINT",FACE,{"disambiguationData":[TD([[makeQuery(id+"F0.imprint","IMPRINT",EDGE,{"derivedFrom":subQ4}),-1.0]])]});}
            var Q20;
            {var subQ0=sQuery(id+"F0.wireOp",EDGE,"E70");Q20=makeQuery(id+"F0.imprint","IMPRINT",FACE,{"disambiguationData":[TD([[makeQuery(id+"F0.imprint","IMPRINT",EDGE,{"derivedFrom":subQ0}),-1.0]])]});}
            var Q21;
            {var subQ0=sQuery(id+"F0.wireOp",EDGE,"E60.MirrorCS");Q21=makeQuery(id+"F0.imprint","IMPRINT",FACE,{"disambiguationData":[TD([[makeQuery(id+"F0.imprint","IMPRINT",EDGE,{"derivedFrom":subQ0}),1.0]])]});}
            var Q22;
            {var subQ0=sQuery(id+"F0.wireOp",EDGE,"E44.MirrorCS");Q22=makeQuery(id+"F0.imprint","IMPRINT",FACE,{"disambiguationData":[TD([[makeQuery(id+"F0.imprint","IMPRINT",EDGE,{"derivedFrom":subQ0}),-1.0]])]});}
            var Q23;
            {var subQ0=sQuery(id+"F0.wireOp",EDGE,"E3.bottom");Q23=makeQuery(id+"F0.imprint","IMPRINT",FACE,{"disambiguationData":[TD([[makeQuery(id+"F0.imprint","IMPRINT",EDGE,{"derivedFrom":subQ0}),-1.0]])]});}
            var Q24;
            {var subQ6=sQuery(id+"F0.wireOp",EDGE,"E18");Q24=makeQuery(id+"F0.imprint","IMPRINT",FACE,{"disambiguationData":[TD([[makeQuery(id+"F0.imprint","IMPRINT",EDGE,{"derivedFrom":subQ6}),-1.0]])]});}
            var Q25;
            {var subQ3=sQuery(id+"F0.wireOp",EDGE,"E51");Q25=makeQuery(id+"F0.imprint","IMPRINT",FACE,{"disambiguationData":[TD([[makeQuery(id+"F0.imprint","IMPRINT",EDGE,{"derivedFrom":subQ3}),-1.0]])]});}
            var Q26;
            {var subQ1=sQuery(id+"F0.wireOp",EDGE,"tfAmf85F-RHVb-4QbN-3uL9-GZ0NnuUHbLcj.left");Q26=makeQuery(id+"F0.imprint","IMPRINT",FACE,{"disambiguationData":[TD([[makeQuery(id+"F0.imprint","IMPRINT",EDGE,{"derivedFrom":subQ1}),-1.0]])]});}
            var Q27;
            {var subQ5=sQuery(id+"F0.wireOp",EDGE,"E144.right");Q27=makeQuery(id+"F0.imprint","IMPRINT",FACE,{"disambiguationData":[TD([[makeQuery(id+"F0.imprint","IMPRINT",EDGE,{"derivedFrom":subQ5}),-1.0]])]});}
            var Q28;
            {var subQ5=sQuery(id+"F0.wireOp",EDGE,"E148.MirrorCS");Q28=makeQuery(id+"F0.imprint","IMPRINT",FACE,{"disambiguationData":[TD([[makeQuery(id+"F0.imprint","IMPRINT",EDGE,{"derivedFrom":subQ5}),1.0]])]});}
            var Q29;
            {var subQ5=sQuery(id+"F0.wireOp",EDGE,"40aa9182-da7a-4239-aef8-64ec93e78b944.MirrorCS");Q29=makeQuery(id+"F0.imprint","IMPRINT",FACE,{"disambiguationData":[TD([[makeQuery(id+"F0.imprint","IMPRINT",EDGE,{"derivedFrom":subQ5}),1.0]])]});}
            var Q30;
            Q30=makeQuery(id+"F0.imprint","IMPRINT",FACE,{"disambiguationData":[TD([[makeQuery(id+"F0.imprint","IMPRINT",EDGE,{"derivedFrom":sQuery(id+"F0.wireOp",EDGE,"E163.bottom")}),-1.0]])]});
            extrude(context, id + "F1", {"entities" : qUnion([Q0, Q1, Q2, Q3, Q4, Q5, Q6, Q7, Q8, Q9, Q10, Q11, Q12, Q13, Q14, Q15, Q16, Q17, Q18, Q19, Q20, Q21, Q22, Q23, Q24, Q25, Q26, Q27, Q28, Q29, Q30]), "depth" : 4 * mm});
        }
        {
            var Q0;
            {var subQ5=sQuery(id+"F0.wireOp",EDGE,"E18");Q0=makeQuery(id+"F0.imprint","IMPRINT",FACE,{"disambiguationData":[TD([[makeQuery(id+"F0.imprint","IMPRINT",EDGE,{"derivedFrom":subQ5}),-1.0]])]});}
            var Q1;
            {var subQ0=sQuery(id+"F0.wireOp",EDGE,"E54");Q1=makeQuery(id+"F0.imprint","IMPRINT",FACE,{"disambiguationData":[TD([[makeQuery(id+"F0.imprint","IMPRINT",EDGE,{"derivedFrom":subQ0}),1.0]])]});}
            var Q2;
            {var subQ0=sQuery(id+"F0.wireOp",EDGE,"E47");var subQ1=sQuery(id+"F0.wireOp",EDGE,"E45");var subQ2=makeQuery(id+"F0.imprint","INTERSECT",VERTEX,{"derivedFrom":[subQ1,subQ0]});Q2=makeQuery(id+"F0.imprint","IMPRINT",FACE,{"disambiguationData":[TD([[makeQuery(id+"F0.imprint","IMPRINT",EDGE,{"disambiguationData":[TD([[subQ2,-1.0]])],"derivedFrom":subQ1}),1.0]])]});}
            var Q3;
            {var subQ0=sQuery(id+"F0.wireOp",EDGE,"E47");var subQ1=sQuery(id+"F0.wireOp",EDGE,"E45");var subQ2=makeQuery(id+"F0.imprint","INTERSECT",VERTEX,{"derivedFrom":[subQ1,subQ0]});Q3=makeQuery(id+"F0.imprint","IMPRINT",FACE,{"disambiguationData":[TD([[makeQuery(id+"F0.imprint","IMPRINT",EDGE,{"disambiguationData":[TD([[subQ2,-1.0]])],"derivedFrom":subQ1}),-1.0]])]});}
            var Q4;
            {var subQ0=sQuery(id+"F0.wireOp",EDGE,"E44.MirrorCS");Q4=makeQuery(id+"F0.imprint","IMPRINT",FACE,{"disambiguationData":[TD([[makeQuery(id+"F0.imprint","IMPRINT",EDGE,{"derivedFrom":subQ0}),-1.0]])]});}
            var Q5;
            {var subQ0=sQuery(id+"F0.wireOp",EDGE,"E62.MirrorCS");Q5=makeQuery(id+"F0.imprint","IMPRINT",FACE,{"disambiguationData":[TD([[makeQuery(id+"F0.imprint","IMPRINT",EDGE,{"derivedFrom":subQ0}),-1.0]])]});}
            var Q6;
            {var subQ0=sQuery(id+"F0.wireOp",EDGE,"E60.MirrorCS");Q6=makeQuery(id+"F0.imprint","IMPRINT",FACE,{"disambiguationData":[TD([[makeQuery(id+"F0.imprint","IMPRINT",EDGE,{"derivedFrom":subQ0}),1.0]])]});}
            extrude(context, id + "F2", {"entities" : qUnion([Q0, Q1, Q2, Q3, Q4, Q5, Q6]), "depth" : 4 * mm});
        }
        {
            var Q0;
            {var subQ1=sQuery(id+"F0.wireOp",EDGE,"E45");var subQ3=sQuery(id+"F0.wireOp",EDGE,"E47");var subQ4=makeQuery(id+"F0.imprint","INTERSECT",VERTEX,{"derivedFrom":[subQ1,subQ3]});Q0=makeQuery(id+"F0.imprint","IMPRINT",FACE,{"disambiguationData":[TD([[makeQuery(id+"F0.imprint","IMPRINT",EDGE,{"disambiguationData":[TD([[subQ4,1.0]])],"derivedFrom":subQ3}),-1.0]])]});}
            var Q1;
            {var subQ1=sQuery(id+"F0.wireOp",EDGE,"E12");Q1=makeQuery(id+"F0.imprint","IMPRINT",FACE,{"disambiguationData":[TD([[makeQuery(id+"F0.imprint","IMPRINT",EDGE,{"derivedFrom":subQ1}),1.0]])]});}
            var Q2;
            {var subQ0=sQuery(id+"F0.wireOp",EDGE,"E53");Q2=makeQuery(id+"F0.imprint","IMPRINT",FACE,{"disambiguationData":[TD([[makeQuery(id+"F0.imprint","IMPRINT",EDGE,{"derivedFrom":subQ0}),1.0]])]});}
            var Q3;
            {var subQ0=sQuery(id+"F0.wireOp",EDGE,"E47");var subQ1=sQuery(id+"F0.wireOp",EDGE,"E45");var subQ2=makeQuery(id+"F0.imprint","INTERSECT",VERTEX,{"derivedFrom":[subQ1,subQ0]});Q3=makeQuery(id+"F0.imprint","IMPRINT",FACE,{"disambiguationData":[TD([[makeQuery(id+"F0.imprint","IMPRINT",EDGE,{"disambiguationData":[TD([[subQ2,-1.0]])],"derivedFrom":subQ1}),1.0]])]});}
            var Q4;
            {var subQ0=sQuery(id+"F0.wireOp",EDGE,"E11.MirrorCS");Q4=makeQuery(id+"F0.imprint","IMPRINT",FACE,{"disambiguationData":[TD([[makeQuery(id+"F0.imprint","IMPRINT",EDGE,{"derivedFrom":subQ0}),-1.0]])]});}
            var Q5;
            Q5=makeQuery(id+"F0.imprint","IMPRINT",FACE,{"disambiguationData":[TD([[makeQuery(id+"F0.imprint","IMPRINT",EDGE,{"derivedFrom":sQuery(id+"F0.wireOp",EDGE,"E11.MirrorCS")}),1.0]])]});
            var Q6;
            {var subQ0=sQuery(id+"F0.wireOp",EDGE,"E70");Q6=makeQuery(id+"F0.imprint","IMPRINT",FACE,{"disambiguationData":[TD([[makeQuery(id+"F0.imprint","IMPRINT",EDGE,{"derivedFrom":subQ0}),-1.0]])]});}
            var Q7;
            {var subQ0=sQuery(id+"F0.wireOp",EDGE,"E66.MirrorCS");Q7=makeQuery(id+"F0.imprint","IMPRINT",FACE,{"disambiguationData":[TD([[makeQuery(id+"F0.imprint","IMPRINT",EDGE,{"derivedFrom":subQ0}),-1.0]])]});}
            extrude(context, id + "F3", {"entities" : qUnion([Q0, Q1, Q2, Q3, Q4, Q5, Q6, Q7]), "depth" : 4 * mm});
        }
        {
            var Q0;
            Q0=makeQuery(id+"F0.imprint","IMPRINT",FACE,{"disambiguationData":[TD([[makeQuery(id+"F0.imprint","IMPRINT",EDGE,{"derivedFrom":sQuery(id+"F0.wireOp",EDGE,"E80")}),1.0]])]});
            var Q1;
            Q1=makeQuery(id+"F0.imprint","IMPRINT",FACE,{"disambiguationData":[TD([[makeQuery(id+"F0.imprint","IMPRINT",EDGE,{"derivedFrom":sQuery(id+"F0.wireOp",EDGE,"E4")}),1.0]])]});
            var Q2;
            Q2=makeQuery(id+"F0.imprint","IMPRINT",FACE,{"disambiguationData":[TD([[makeQuery(id+"F0.imprint","IMPRINT",EDGE,{"derivedFrom":sQuery(id+"F0.wireOp",EDGE,"E95")}),-1.0]])]});
            var Q3;
            {var subQ1=sQuery(id+"F0.wireOp",EDGE,"E173");Q3=makeQuery(id+"F0.imprint","IMPRINT",FACE,{"disambiguationData":[TD([[makeQuery(id+"F0.imprint","IMPRINT",EDGE,{"derivedFrom":subQ1}),1.0]])]});}
            var Q4;
            {var subQ0=sQuery(id+"F0.wireOp",EDGE,"r6UPohRk-UKm2-Sz1P-ikt3-u7nHveilahU9");Q4=makeQuery(id+"F0.imprint","IMPRINT",FACE,{"disambiguationData":[TD([[makeQuery(id+"F0.imprint","IMPRINT",EDGE,{"derivedFrom":subQ0}),-1.0]])]});}
            var Q5;
            {var subQ0=sQuery(id+"F0.wireOp",EDGE,"w7t8HZqR-IddA-Lt6B-wytb-2f7laMw5EWdT");Q5=makeQuery(id+"F0.imprint","IMPRINT",FACE,{"disambiguationData":[TD([[makeQuery(id+"F0.imprint","IMPRINT",EDGE,{"derivedFrom":subQ0}),1.0]])]});}
            var Q6;
            {var subQ0=sQuery(id+"F0.wireOp",EDGE,"w7t8HZqR-IddA-Lt6B-wytb-2f7laMw5EWdT");Q6=makeQuery(id+"F0.imprint","IMPRINT",FACE,{"disambiguationData":[TD([[makeQuery(id+"F0.imprint","IMPRINT",EDGE,{"derivedFrom":subQ0}),-1.0]])]});}
            extrude(context, id + "F4", {"entities" : qUnion([Q0, Q1, Q2, Q3, Q4, Q5, Q6]), "depth" : 4 * mm});
        }
        {
            var Q0;
            Q0=makeQuery(id+"F0.imprint","IMPRINT",FACE,{"disambiguationData":[TD([[makeQuery(id+"F0.imprint","IMPRINT",EDGE,{"derivedFrom":sQuery(id+"F0.wireOp",EDGE,"E126")}),-1.0]])]});
            var Q1;
            {var subQ0=sQuery(id+"F0.wireOp",EDGE,"E100");Q1=makeQuery(id+"F0.imprint","IMPRINT",FACE,{"disambiguationData":[TD([[makeQuery(id+"F0.imprint","IMPRINT",EDGE,{"derivedFrom":subQ0}),1.0]])]});}
            var Q2;
            Q2=makeQuery(id+"F0.imprint","IMPRINT",FACE,{"disambiguationData":[TD([[makeQuery(id+"F0.imprint","IMPRINT",EDGE,{"derivedFrom":sQuery(id+"F0.wireOp",EDGE,"E132")}),1.0]])]});
            extrude(context, id + "F5", {"entities" : qUnion([Q0, Q1, Q2]), "depth" : 4 * mm});
        }
        {
            var Q0;
            Q0=makeQuery(id+"F2.opExtrude","SWEPT_FACE",FACE,{"disambiguationData":[OSD([sQuery(id+"F0.wireOp",EDGE,"E161.right")])]});
            var sketch = newSketch(context, id + "F6", { "sketchPlane" : qUnion([Q0])});
            skLineSegment(sketch, "E215.bottom", {"start": v(-94.84, 0) * mm, "end": v(-92.84, 0) * mm});
            skLineSegment(sketch, "E215.top", {"start": v(-96.84, 10) * mm, "end": v(-92.84, 10) * mm});
            skLineSegment(sketch, "E216.bottom", {"start": v(-88.84, 4) * mm, "end": v(108, 4) * mm});
            skLineSegment(sketch, "E216.top", {"start": v(-92.84, 10) * mm, "end": v(112, 10) * mm});
            skLineSegment(sketch, "E216.right", {"start": v(112, 4) * mm, "end": v(112, 10) * mm});
            skLineSegment(sketch, "E217.0.1", {"start": v(112, 0) * mm, "end": v(112, 4) * mm});
            skLineSegment(sketch, "E217.0.3", {"start": v(108, 4) * mm, "end": v(108, 0) * mm});
            skPoint(sketch, "E217.0.2.end.orphan", {"position": v(108, 4) * mm});
            skLineSegment(sketch, "E218.top", {"start": v(-96.84, -10) * mm, "end": v(-92.84, -10) * mm});
            skLineSegment(sketch, "E218.left", {"start": v(-96.84, 0) * mm, "end": v(-96.84, -10) * mm});
            skLineSegment(sketch, "E218.right", {"start": v(-92.84, 0) * mm, "end": v(-92.84, -10) * mm});
            skPoint(sketch, "E219.oppositeSnap0", {"position": v(-94.84, 0) * mm});
            skFitSpline(sketch, "E220", {"points": [v(-96.84, 10) * mm, v(-100.84, 4) * mm], "startDerivative": vector(-4.3, 0.57) * mm, "endDerivative": vector(1.18, -14.2) * mm});
            skLineSegment(sketch, "E221", {"start": v(112, 4) * mm, "end": v(117.7, 4) * mm});
            skLineSegment(sketch, "E222", {"start": v(108, 0) * mm, "end": v(108, -10) * mm});
            skLineSegment(sketch, "E223", {"start": v(108, -10) * mm, "end": v(112, -10) * mm});
            skLineSegment(sketch, "E224", {"start": v(112, -10) * mm, "end": v(112, 0) * mm});
            skFitSpline(sketch, "E225", {"points": [v(112, 10) * mm, v(117.7, 4) * mm], "startDerivative": vector(11.43, 0.2) * mm, "endDerivative": vector(0.16, -10.43) * mm});
            skPoint(sketch, "E219.right.end.orphan", {"position": v(-100.84, 0) * mm});
            skLineSegment(sketch, "E226", {"start": v(-100.84, 4) * mm, "end": v(-100.84, 2) * mm});
            skLineSegment(sketch, "E227", {"start": v(-100.84, 2) * mm, "end": v(-96.84, 2) * mm});
            skLineSegment(sketch, "E228", {"start": v(-88.84, 2) * mm, "end": v(-88.84, 4) * mm});
            skLineSegment(sketch, "E229", {"start": v(-92.84, 0) * mm, "end": v(-92.84, 2) * mm});
            skLineSegment(sketch, "E230", {"start": v(-96.84, 0) * mm, "end": v(-96.84, 2) * mm});
            skLineSegment(sketch, "E231.trimOffspring", {"start": v(-92.84, 2) * mm, "end": v(-88.84, 2) * mm});
            skLineSegment(sketch, "E232", {"start": v(-100.84, 2) * mm, "end": v(-100.84, 0) * mm});
            skLineSegment(sketch, "E233", {"start": v(-88.84, 2) * mm, "end": v(-88.84, 0) * mm});
            skLineSegment(sketch, "E234", {"start": v(-88.84, 0) * mm, "end": v(-100.84, 0) * mm});
            skLineSegment(sketch, "E235", {"start": v(-100.84, 0) * mm, "end": v(-100.84, -2) * mm});
            skLineSegment(sketch, "E236", {"start": v(-100.84, -2) * mm, "end": v(-88.84, -2) * mm});
            skLineSegment(sketch, "E237", {"start": v(-88.84, -2) * mm, "end": v(-88.84, 0) * mm});
            skLineSegment(sketch, "E238.top", {"start": v(-60.3, -170.8) * mm, "end": v(-56.3, -170.8) * mm});
            skLineSegment(sketch, "E239.bottom", {"start": v(-52.3, -176.8) * mm, "end": v(144.55, -176.8) * mm});
            skLineSegment(sketch, "E239.top", {"start": v(-56.3, -170.8) * mm, "end": v(148.55, -170.8) * mm});
            skLineSegment(sketch, "E240.0.1", {"start": v(148.55, -180.8) * mm, "end": v(148.55, -176.8) * mm});
            skLineSegment(sketch, "E240.0.3", {"start": v(144.55, -176.8) * mm, "end": v(144.55, -180.8) * mm});
            skPoint(sketch, "E240.0.2.end.orphan", {"position": v(144.55, -176.8) * mm});
            skLineSegment(sketch, "E241.top", {"start": v(-60.3, -190.8) * mm, "end": v(-56.3, -190.8) * mm});
            skLineSegment(sketch, "E241.left", {"start": v(-60.3, -182.8) * mm, "end": v(-60.3, -190.8) * mm});
            skLineSegment(sketch, "E241.right", {"start": v(-56.3, -182.8) * mm, "end": v(-56.3, -190.8) * mm});
            skPoint(sketch, "E242.oppositeSnap0", {"position": v(-58.3, -180.8) * mm});
            skFitSpline(sketch, "E243", {"points": [v(-60.3, -170.8) * mm, v(-64.3, -176.8) * mm], "startDerivative": vector(-4.3, 0.57) * mm, "endDerivative": vector(1.18, -14.2) * mm});
            skLineSegment(sketch, "E244", {"start": v(148.55, -176.8) * mm, "end": v(154.24, -176.8) * mm});
            skLineSegment(sketch, "E245", {"start": v(144.55, -180.8) * mm, "end": v(144.55, -190.8) * mm});
            skLineSegment(sketch, "E246", {"start": v(144.55, -190.8) * mm, "end": v(148.55, -190.8) * mm});
            skLineSegment(sketch, "E247", {"start": v(148.55, -190.8) * mm, "end": v(148.55, -180.8) * mm});
            skFitSpline(sketch, "E248", {"points": [v(148.55, -170.8) * mm, v(154.24, -176.8) * mm], "startDerivative": vector(11.43, 0.2) * mm, "endDerivative": vector(0.16, -10.43) * mm});
            skPoint(sketch, "E242.right.end.orphan", {"position": v(-64.3, -180.8) * mm});
            skLineSegment(sketch, "E249", {"start": v(-64.3, -176.8) * mm, "end": v(-64.3, -178.8) * mm});
            skLineSegment(sketch, "E250", {"start": v(-52.3, -178.8) * mm, "end": v(-52.3, -176.8) * mm});
            skLineSegment(sketch, "E251", {"start": v(-64.3, -178.8) * mm, "end": v(-64.3, -180.8) * mm});
            skLineSegment(sketch, "E252", {"start": v(-52.3, -178.8) * mm, "end": v(-52.3, -180.8) * mm});
            skLineSegment(sketch, "E253", {"start": v(-64.3, -180.8) * mm, "end": v(-64.3, -182.8) * mm});
            skLineSegment(sketch, "E254", {"start": v(-64.3, -182.8) * mm, "end": v(-60.3, -182.8) * mm});
            skLineSegment(sketch, "E255", {"start": v(-52.3, -182.8) * mm, "end": v(-52.3, -180.8) * mm});
            skPoint(sketch, "E238.bottom.end.orphan", {"position": v(-56.3, -180.8) * mm});
            skPoint(sketch, "E256.end.orphan", {"position": v(-60.3, -180.8) * mm});
            skLineSegment(sketch, "E257.trimOffspring", {"start": v(-56.3, -182.8) * mm, "end": v(-52.3, -182.8) * mm});
            skSolve(sketch);
        }
        {
            var Q0;
            Q0=qSketchRegion(id+"F6",true);
            extrude(context, id + "F7", {"entities" : qUnion([Q0]), "depth" : 3 * mm});
        }
        {
            var Q0;
            {var subQ4=sQuery(id+"F0.wireOp",EDGE,"E164.top");Q0=makeQuery(id+"F0.imprint","IMPRINT",FACE,{"disambiguationData":[TD([[makeQuery(id+"F0.imprint","IMPRINT",EDGE,{"derivedFrom":subQ4}),-1.0]])]});}
            var Q1;
            {var subQ5=sQuery(id+"F0.wireOp",EDGE,"E165.top");Q1=makeQuery(id+"F0.imprint","IMPRINT",FACE,{"disambiguationData":[TD([[makeQuery(id+"F0.imprint","IMPRINT",EDGE,{"derivedFrom":subQ5}),1.0]])]});}
            var Q2;
            {var subQ5=sQuery(id+"F0.wireOp",EDGE,"E165.bottom");Q2=makeQuery(id+"F0.imprint","IMPRINT",FACE,{"disambiguationData":[TD([[makeQuery(id+"F0.imprint","IMPRINT",EDGE,{"derivedFrom":subQ5}),-1.0]])]});}
            var Q3;
            Q3=makeQuery(id+"F0.imprint","IMPRINT",FACE,{"disambiguationData":[TD([[makeQuery(id+"F0.imprint","IMPRINT",EDGE,{"derivedFrom":sQuery(id+"F0.wireOp",EDGE,"E165.bottom")}),1.0]])]});
            extrude(context, id + "F8", {"entities" : qUnion([Q0, Q1, Q2, Q3]), "depth" : 3 * mm});
        }
        {
            var Q0;
            {var subQ1=sQuery(id+"F0.wireOp",EDGE,"E173");Q0=makeQuery(id+"F0.imprint","IMPRINT",FACE,{"disambiguationData":[TD([[makeQuery(id+"F0.imprint","IMPRINT",EDGE,{"derivedFrom":subQ1}),1.0]])]});}
            var Q1;
            {var subQ0=sQuery(id+"F0.wireOp",EDGE,"E177");Q1=makeQuery(id+"F0.imprint","IMPRINT",FACE,{"disambiguationData":[TD([[makeQuery(id+"F0.imprint","IMPRINT",EDGE,{"derivedFrom":subQ0}),1.0]])]});}
            var Q2;
            {var subQ0=sQuery(id+"F0.wireOp",EDGE,"r6UPohRk-UKm2-Sz1P-ikt3-u7nHveilahU9");Q2=makeQuery(id+"F0.imprint","IMPRINT",FACE,{"disambiguationData":[TD([[makeQuery(id+"F0.imprint","IMPRINT",EDGE,{"derivedFrom":subQ0}),-1.0]])]});}
            var Q3;
            {var subQ1=sQuery(id+"F0.wireOp",EDGE,"E186");Q3=makeQuery(id+"F0.imprint","IMPRINT",FACE,{"disambiguationData":[TD([[makeQuery(id+"F0.imprint","IMPRINT",EDGE,{"derivedFrom":subQ1}),1.0]])]});}
            var Q4;
            {var subQ0=sQuery(id+"F0.wireOp",EDGE,"w7t8HZqR-IddA-Lt6B-wytb-2f7laMw5EWdT");Q4=makeQuery(id+"F0.imprint","IMPRINT",FACE,{"disambiguationData":[TD([[makeQuery(id+"F0.imprint","IMPRINT",EDGE,{"derivedFrom":subQ0}),1.0]])]});}
            var Q5;
            {var subQ0=sQuery(id+"F0.wireOp",EDGE,"w7t8HZqR-IddA-Lt6B-wytb-2f7laMw5EWdT");Q5=makeQuery(id+"F0.imprint","IMPRINT",FACE,{"disambiguationData":[TD([[makeQuery(id+"F0.imprint","IMPRINT",EDGE,{"derivedFrom":subQ0}),-1.0]])]});}
            extrude(context, id + "F9", {"entities" : qUnion([Q0, Q1, Q2, Q3, Q4, Q5]), "depth" : 8 * mm});
        }
        {
            var Q0;
            {var subQ4=sQuery(id+"F0.wireOp",EDGE,"42LOBuK3-sroH-6gsT-vy40-p2PcoGOjGRd3.bottom");Q0=makeQuery(id+"F0.imprint","IMPRINT",FACE,{"disambiguationData":[TD([[makeQuery(id+"F0.imprint","IMPRINT",EDGE,{"derivedFrom":subQ4}),-1.0]])]});}
            var Q1;
            {var subQ0=sQuery(id+"F0.wireOp",EDGE,"E213.MirrorCS");Q1=makeQuery(id+"F0.imprint","IMPRINT",FACE,{"disambiguationData":[TD([[makeQuery(id+"F0.imprint","IMPRINT",EDGE,{"derivedFrom":subQ0}),-1.0]])]});}
            var Q2;
            {var subQ0=sQuery(id+"F0.wireOp",EDGE,"E212");Q2=makeQuery(id+"F0.imprint","IMPRINT",FACE,{"disambiguationData":[TD([[makeQuery(id+"F0.imprint","IMPRINT",EDGE,{"derivedFrom":subQ0}),1.0]])]});}
            var Q3;
            {var subQ1=sQuery(id+"F0.wireOp",EDGE,"E179");var subQ3=makeQuery(id+"F0.imprint","IMPRINT",VERTEX,{"derivedFrom":subQ1});Q3=makeQuery(id+"F0.imprint","IMPRINT",FACE,{"disambiguationData":[TD([[makeQuery(id+"F0.imprint","IMPRINT",EDGE,{"disambiguationData":[TD([[subQ3,-1.0]])],"derivedFrom":subQ1}),-1.0]])]});}
            var Q4;
            Q4=makeQuery(id+"F0.imprint","IMPRINT",FACE,{"disambiguationData":[TD([[makeQuery(id+"F0.imprint","IMPRINT",EDGE,{"derivedFrom":sQuery(id+"F0.wireOp",EDGE,"42LOBuK3-sroH-6gsT-vy40-p2PcoGOjGRd3.top")}),-1.0]])]});
            var Q5;
            Q5=makeQuery(id+"F0.imprint","IMPRINT",FACE,{"disambiguationData":[TD([[makeQuery(id+"F0.imprint","IMPRINT",EDGE,{"derivedFrom":sQuery(id+"F0.wireOp",EDGE,"E178.bottom")}),-1.0]])]});
            var Q6;
            {var subQ0=sQuery(id+"F0.wireOp",EDGE,"E180");Q6=makeQuery(id+"F0.imprint","IMPRINT",FACE,{"disambiguationData":[TD([[makeQuery(id+"F0.imprint","IMPRINT",EDGE,{"derivedFrom":subQ0}),1.0]])]});}
            extrude(context, id + "F10", {"entities" : qUnion([Q0, Q1, Q2, Q3, Q4, Q5, Q6]), "depth" : 8 * mm});
        }
    });
